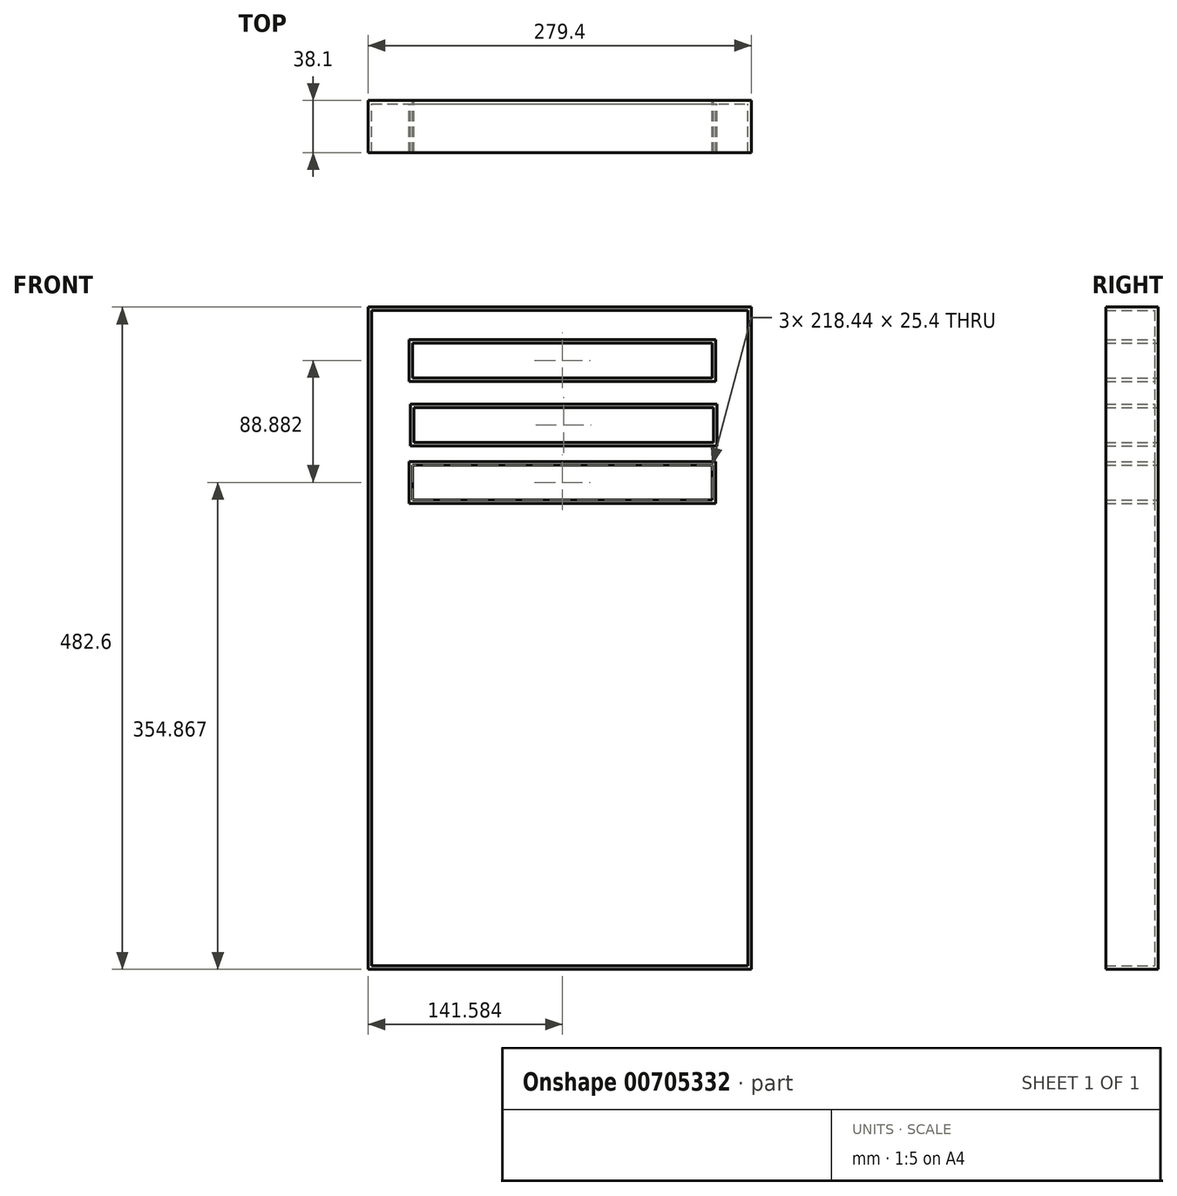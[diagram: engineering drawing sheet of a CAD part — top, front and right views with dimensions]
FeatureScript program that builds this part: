
annotation { "Feature Type Name" : "Feature", "Feature Type Description" : "" }
export const myFeature = defineFeature(function(context is Context, id is Id, definition is map)
    precondition{}
    {
        {
            var Q0;
            Q0=qCreatedBy(makeId("Front.planeOp"),FACE);
            var sketch = newSketch(context, id + "F0", { "sketchPlane" : qUnion([Q0])});
            skLineSegment(sketch, "E0.bottom", {"start": v(-174.3, 241.48) * mm, "end": v(105.1, 241.48) * mm});
            skLineSegment(sketch, "E0.top", {"start": v(-174.3, -241.12) * mm, "end": v(105.1, -241.12) * mm});
            skLineSegment(sketch, "E0.left", {"start": v(-174.3, 241.48) * mm, "end": v(-174.3, -241.12) * mm});
            skLineSegment(sketch, "E0.right", {"start": v(105.1, 241.48) * mm, "end": v(105.1, -241.12) * mm});
            skLineSegment(sketch, "E1.bottom", {"start": v(-141.94, 215.33) * mm, "end": v(76.5, 215.33) * mm});
            skLineSegment(sketch, "E1.top", {"start": v(-141.94, 189.93) * mm, "end": v(76.5, 189.93) * mm});
            skLineSegment(sketch, "E1.left", {"start": v(-141.94, 215.33) * mm, "end": v(-141.94, 189.93) * mm});
            skLineSegment(sketch, "E1.right", {"start": v(76.5, 215.33) * mm, "end": v(76.5, 189.93) * mm});
            skLineSegment(sketch, "E2.bottom", {"start": v(-141.05, 168.22) * mm, "end": v(77.4, 168.22) * mm});
            skLineSegment(sketch, "E2.top", {"start": v(-141.05, 142.82) * mm, "end": v(77.4, 142.82) * mm});
            skLineSegment(sketch, "E2.left", {"start": v(-141.05, 168.22) * mm, "end": v(-141.05, 142.82) * mm});
            skLineSegment(sketch, "E2.right", {"start": v(77.4, 168.22) * mm, "end": v(77.4, 142.82) * mm});
            skLineSegment(sketch, "E3.bottom", {"start": v(-141.94, 126.45) * mm, "end": v(76.5, 126.45) * mm});
            skLineSegment(sketch, "E3.top", {"start": v(-141.94, 101.05) * mm, "end": v(76.5, 101.05) * mm});
            skLineSegment(sketch, "E3.left", {"start": v(-141.94, 126.45) * mm, "end": v(-141.94, 101.05) * mm});
            skLineSegment(sketch, "E3.right", {"start": v(76.5, 126.45) * mm, "end": v(76.5, 101.05) * mm});
            skSolve(sketch);
        }
        {
            var Q0;
            Q0 = qSketchRegion(id + "F0", true);
            extrude(context, id + "F1", {"entities" : qUnion([Q0]), "depth" : 38.1 * mm, "offsetDistance" : 25.4 * mm});
        }
        {
            var Q0;
            Q0 = qSketchRegion(id + "F0", true);
            extrude(context, id + "F2", {"entities" : qUnion([Q0]), "operationType" : NewBodyOperationType.ADD, "depth" : 25.4 * mm, "offsetDistance" : 25.4 * mm});
        }
        {
            var Q0;
            Q0=makeQuery(id+"F1.opExtrude","CAP_FACE",FACE,{"disambiguationData":[OSD([sQuery(id+"F0.wireOp",EDGE,"E0.bottom"),sQuery(id+"F0.wireOp",EDGE,"E0.top"),sQuery(id+"F0.wireOp",EDGE,"E0.left"),sQuery(id+"F0.wireOp",EDGE,"E0.right"),sQuery(id+"F0.wireOp",EDGE,"E1.bottom"),sQuery(id+"F0.wireOp",EDGE,"E1.top"),sQuery(id+"F0.wireOp",EDGE,"E1.left"),sQuery(id+"F0.wireOp",EDGE,"E1.right"),sQuery(id+"F0.wireOp",EDGE,"E2.bottom"),sQuery(id+"F0.wireOp",EDGE,"E2.top"),sQuery(id+"F0.wireOp",EDGE,"E2.left"),sQuery(id+"F0.wireOp",EDGE,"E2.right"),sQuery(id+"F0.wireOp",EDGE,"E3.bottom"),sQuery(id+"F0.wireOp",EDGE,"E3.top"),sQuery(id+"F0.wireOp",EDGE,"E3.left"),sQuery(id+"F0.wireOp",EDGE,"E3.right")])],"isStart":false});
            shell(context, id + "F3", {"entities" : qUnion([Q0]), "thickness" : 2.54 * mm});
        }
    });
